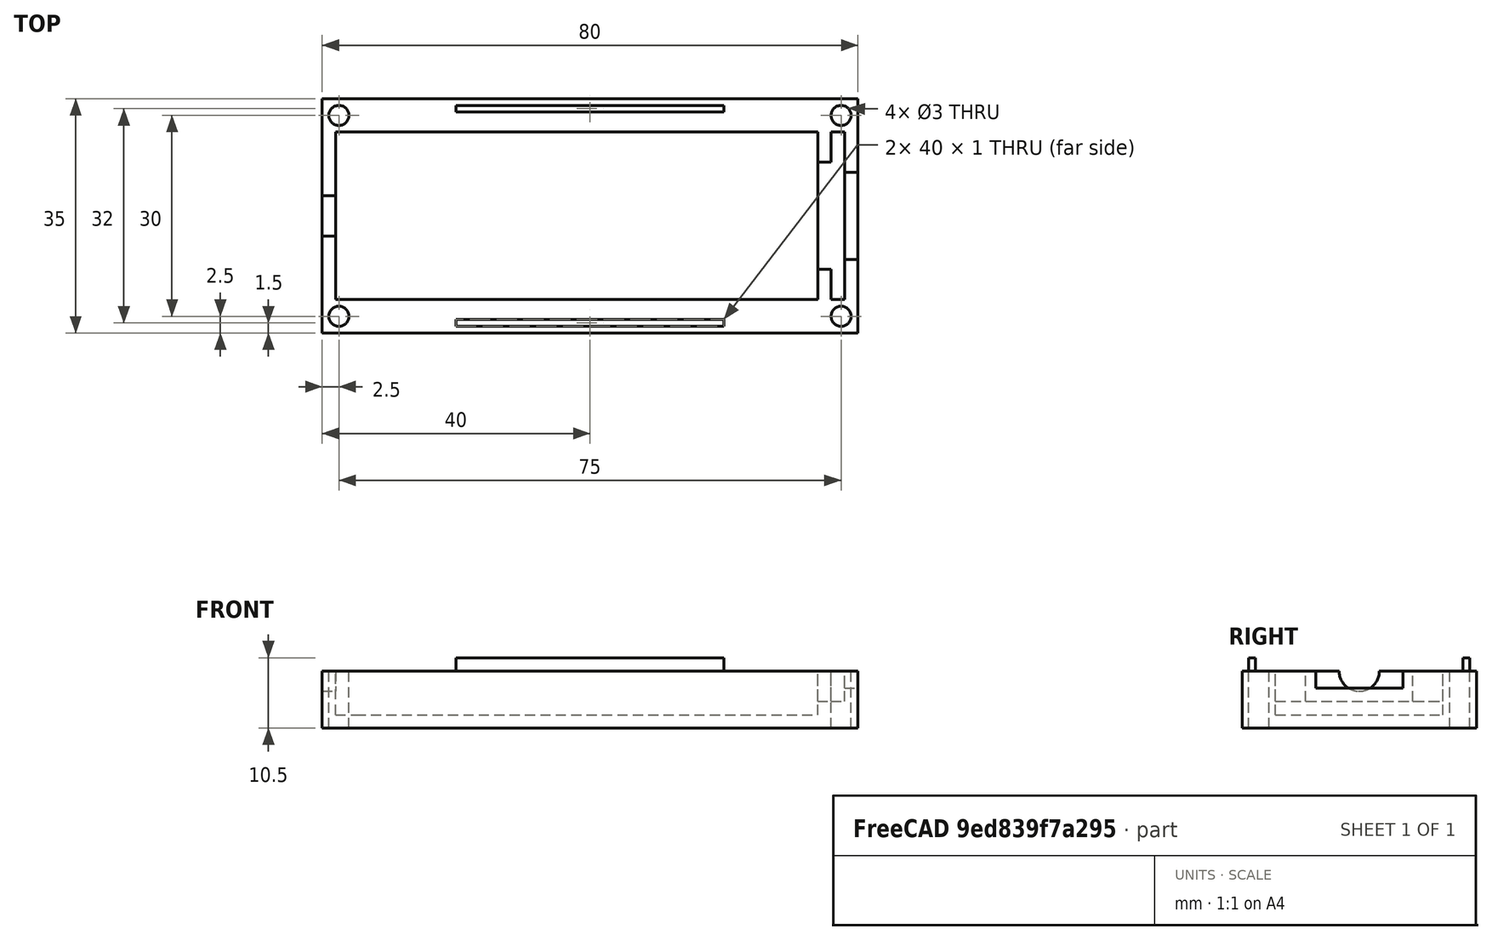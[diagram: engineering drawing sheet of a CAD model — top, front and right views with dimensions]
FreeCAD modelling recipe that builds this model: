
FCSTD DOCUMENT  (FreeCAD 0.17R13509 (Git))
Label: USB2A_2
License: All rights reserved
LicenseURL: http://en.wikipedia.org/wiki/All_rights_reserved
objects: Part::Cut×10, Part::Box×8, Part::Cylinder×5, Part::Fuse×2
note: 25 computed .brp shape members not serialized (recipe doc carries the construction recipe); baked Part::Feature solids carry a one-line shape summary decoded from their .brp

FEATURE [Part::Box] Box  label="外壳"
  AttacherType = Attacher::AttachEngine3D
  Height = 8.5
  Length = 80
  Width = 35
FEATURE [Part::Box] Box001  label="内胆"
  AttacherType = Attacher::AttachEngine3D
  Height = 13
  Length = 69
  Placement = pos=(5,5,2) rot=(0,0,1;0rad)
  Width = 25
FEATURE [Part::Cylinder] Cylinder  label="圆柱体"
  Angle = 360
  AttacherType = Attacher::AttachEngine3D
  Height = 2
  Placement = pos=(0,17.5,8.5) rot=(0,1,0;1.5708rad)
  Radius = 3
FEATURE [Part::Box] Box002  label="卡槽"
  AttacherType = Attacher::AttachEngine3D
  Height = 9
  Length = 2
  Placement = pos=(76,5,4) rot=(0,0,1;0rad)
  Width = 25
FEATURE [Part::Box] Box003  label="U口"
  AttacherType = Attacher::AttachEngine3D
  Height = 5
  Length = 2
  Placement = pos=(78,11,6) rot=(0,0,1;0rad)
  Width = 13
FEATURE [Part::Box] Box004  label="立方体003"
  AttacherType = Attacher::AttachEngine3D
  Height = 9
  Length = 2
  Placement = pos=(74,9.5,4) rot=(0,0,1;0rad)
  Width = 16
FEATURE [Part::Cut] Cut
  Base = -> Box
  Tool = -> Cylinder
FEATURE [Part::Cut] Cut001
  Base = -> Cut
  Tool = -> Box001
FEATURE [Part::Cut] Cut002
  Base = -> Cut001
  Tool = -> Box002
FEATURE [Part::Cut] Cut003
  Base = -> Cut002
  Tool = -> Box003
FEATURE [Part::Cut] Cut004
  Base = -> Cut003
  Tool = -> Box004
FEATURE [Part::Box] Box005  label="立方体"
  AttacherType = Attacher::AttachEngine3D
  Height = 10
  Length = 3
  Placement = pos=(2,5,2) rot=(0,0,1;0rad)
  Width = 25
FEATURE [Part::Cut] Cut005
  Base = -> Cut004
  Tool = -> Box005
FEATURE [Part::Box] Box006  label="卡壁1"
  AttacherType = Attacher::AttachEngine3D
  Height = 10.5
  Length = 40
  Placement = pos=(20,33,0) rot=(0,0,1;0rad)
  Width = 1
FEATURE [Part::Box] Box007  label="卡壁2"
  AttacherType = Attacher::AttachEngine3D
  Height = 10.5
  Length = 40
  Placement = pos=(20,1,0) rot=(0,0,1;0rad)
  Width = 1
FEATURE [Part::Fuse] Fusion
  Base = -> Cut005
  Tool = -> Box006
FEATURE [Part::Fuse] Fusion001
  Base = -> Fusion
  Tool = -> Box007
FEATURE [Part::Cylinder] Cylinder001  label="螺孔1"
  Angle = 360
  AttacherType = Attacher::AttachEngine3D
  Height = 10
  Placement = pos=(2.5,2.5,0) rot=(0,0,1;0rad)
  Radius = 1.5
FEATURE [Part::Cylinder] Cylinder002  label="螺孔2"
  Angle = 360
  AttacherType = Attacher::AttachEngine3D
  Height = 10
  Placement = pos=(77.5,2.5,0) rot=(0,0,1;0rad)
  Radius = 1.5
FEATURE [Part::Cylinder] Cylinder003  label="螺孔3"
  Angle = 360
  AttacherType = Attacher::AttachEngine3D
  Height = 10
  Placement = pos=(77.5,32.5,0) rot=(0,0,1;0rad)
  Radius = 1.5
FEATURE [Part::Cylinder] Cylinder004  label="螺孔4"
  Angle = 360
  AttacherType = Attacher::AttachEngine3D
  Height = 10
  Placement = pos=(2.5,32.5,0) rot=(0,0,1;0rad)
  Radius = 1.5
FEATURE [Part::Cut] Cut006
  Base = -> Fusion001
  Tool = -> Cylinder001
FEATURE [Part::Cut] Cut007
  Base = -> Cut006
  Tool = -> Cylinder002
FEATURE [Part::Cut] Cut008
  Base = -> Cut007
  Tool = -> Cylinder003
FEATURE [Part::Cut] Cut009
  Base = -> Cut008
  Tool = -> Cylinder004
